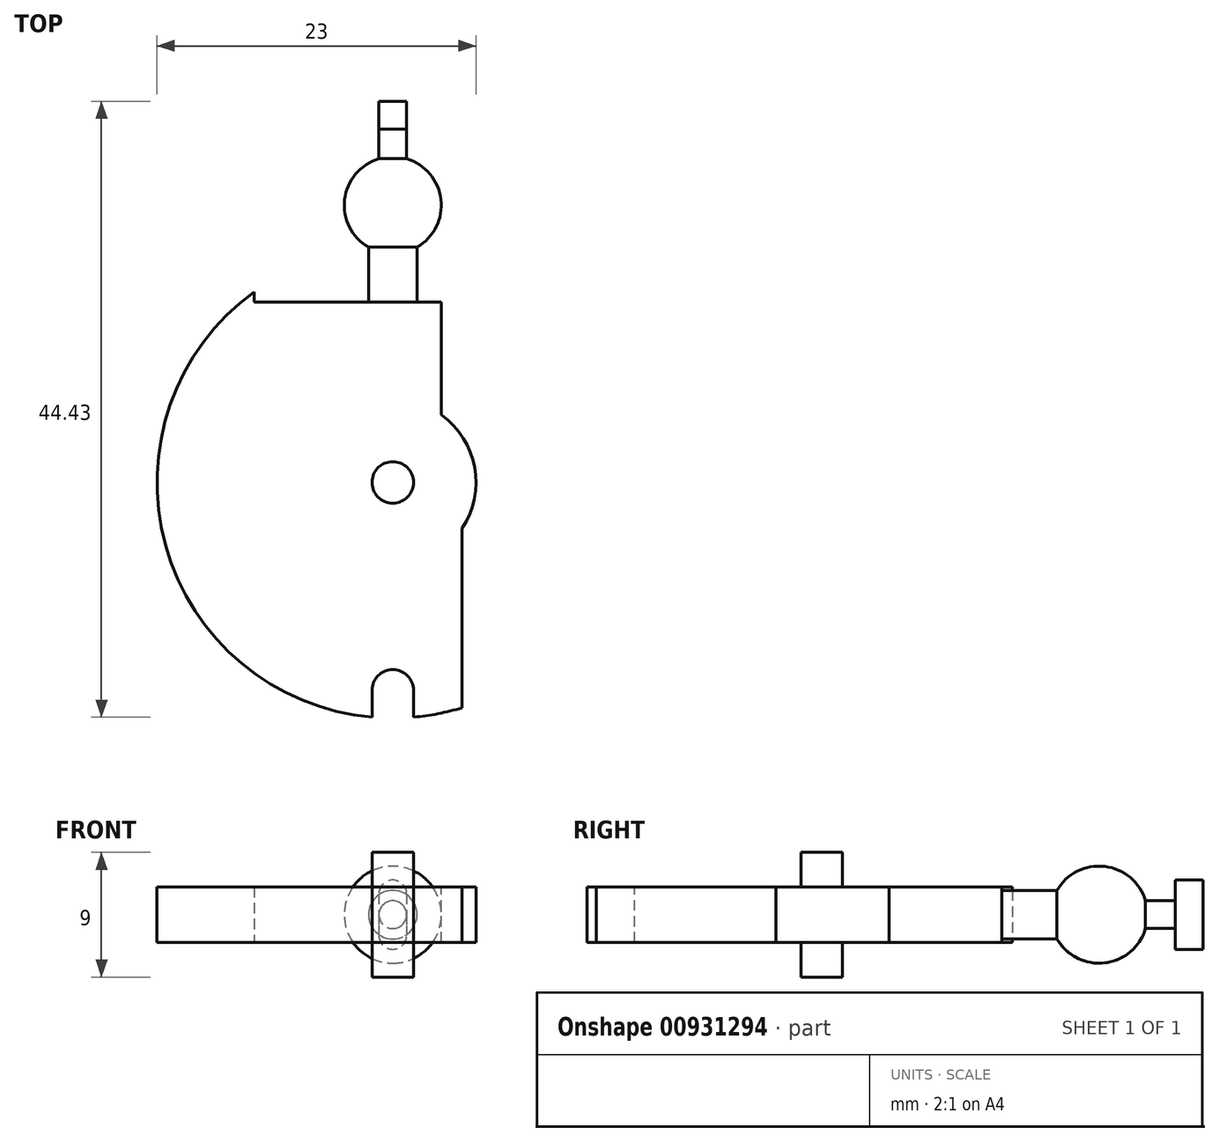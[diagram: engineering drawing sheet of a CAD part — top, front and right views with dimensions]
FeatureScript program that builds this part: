
annotation { "Feature Type Name" : "Feature", "Feature Type Description" : "" }
export const myFeature = defineFeature(function(context is Context, id is Id, definition is map)
    precondition{}
    {
        {
            var Q0;
            Q0=qCreatedBy(makeId("Top.planeOp"),FACE);
            var sketch = newSketch(context, id + "F0", { "sketchPlane" : qUnion([Q0])});
            skCircle(sketch, "E0", {"center": v(0, 0) * mm, "radius": 17 * mm});
            skSolve(sketch);
        }
        {
            var Q0;
            Q0=makeQuery(id+"F0.imprint","IMPRINT",FACE,{"disambiguationData":[TD([[makeQuery(id+"F0.imprint","IMPRINT",EDGE,{"derivedFrom":sQuery(id+"F0.wireOp",EDGE,"E0")}),1.0]])]});
            extrude(context, id + "F1", {"entities" : qUnion([Q0]), "endBound" : BoundingType.SYMMETRIC, "depth" : 4 * mm, "offsetDistance" : 25 * mm});
        }
        {
            var Q0;
            Q0=qCreatedBy(makeId("Top.planeOp"),FACE);
            var sketch = newSketch(context, id + "F2", { "sketchPlane" : qUnion([Q0])});
            skLineSegment(sketch, "E1", {"start": v(-18.14, 0) * mm, "end": v(21.61, 0) * mm, "construction": true});
            skLineSegment(sketch, "E2", {"start": v(0, 15.6) * mm, "end": v(0, -23.05) * mm, "construction": true});
            skLineSegment(sketch, "E3.bottom", {"start": v(5, 0) * mm, "end": v(35, 0) * mm});
            skLineSegment(sketch, "E3.top", {"start": v(5, -30) * mm, "end": v(35, -30) * mm});
            skLineSegment(sketch, "E3.left", {"start": v(5, 0) * mm, "end": v(5, -30) * mm});
            skLineSegment(sketch, "E3.right", {"start": v(35, 0) * mm, "end": v(35, -30) * mm});
            skSolve(sketch);
        }
        {
            var Q0;
            Q0=makeQuery(id+"F2.imprint","IMPRINT",FACE,{"disambiguationData":[TD([[makeQuery(id+"F2.imprint","IMPRINT",EDGE,{"derivedFrom":sQuery(id+"F2.wireOp",EDGE,"E3.bottom")}),-1.0]])]});
            extrude(context, id + "F3", {"entities" : qUnion([Q0]), "operationType" : NewBodyOperationType.REMOVE, "endBound" : BoundingType.SYMMETRIC, "oppositeDirection" : true, "depth" : 25 * mm, "offsetDistance" : 25 * mm});
        }
        {
            var Q0;
            Q0=qCreatedBy(makeId("Top.planeOp"),FACE);
            var sketch = newSketch(context, id + "F4", { "sketchPlane" : qUnion([Q0])});
            skLineSegment(sketch, "E4", {"start": v(-5.74, 0) * mm, "end": v(12.51, 0) * mm, "construction": true});
            skLineSegment(sketch, "E5", {"start": v(0, 9.37) * mm, "end": v(0, -3) * mm, "construction": true});
            skLineSegment(sketch, "E6.bottom", {"start": v(3.5, 30) * mm, "end": v(33.5, 30) * mm});
            skLineSegment(sketch, "E6.top", {"start": v(3.5, 0) * mm, "end": v(33.5, 0) * mm});
            skLineSegment(sketch, "E6.left", {"start": v(3.5, 30) * mm, "end": v(3.5, 0) * mm});
            skLineSegment(sketch, "E6.right", {"start": v(33.5, 30) * mm, "end": v(33.5, 0) * mm});
            skSolve(sketch);
        }
        {
            var Q0;
            Q0=makeQuery(id+"F4.imprint","IMPRINT",FACE,{"disambiguationData":[TD([[makeQuery(id+"F4.imprint","IMPRINT",EDGE,{"derivedFrom":sQuery(id+"F4.wireOp",EDGE,"E6.bottom")}),-1.0]])]});
            extrude(context, id + "F5", {"entities" : qUnion([Q0]), "operationType" : NewBodyOperationType.REMOVE, "endBound" : BoundingType.SYMMETRIC, "oppositeDirection" : true, "depth" : 25 * mm, "offsetDistance" : 25 * mm});
        }
        {
            var Q0;
            Q0=qCreatedBy(makeId("Top.planeOp"),FACE);
            var sketch = newSketch(context, id + "F6", { "sketchPlane" : qUnion([Q0])});
            skCircle(sketch, "E7", {"center": v(0, 0) * mm, "radius": 6 * mm});
            skSolve(sketch);
        }
        {
            var Q0;
            Q0=makeQuery(id+"F6.imprint","IMPRINT",FACE,{"disambiguationData":[TD([[makeQuery(id+"F6.imprint","IMPRINT",EDGE,{"derivedFrom":sQuery(id+"F6.wireOp",EDGE,"E7")}),1.0]])]});
            var Q1;
            Q1=makeQuery(id+"F1.opExtrude","CAP_FACE",FACE,{"disambiguationData":[OSD([sQuery(id+"F0.wireOp",EDGE,"E0")])],"isStart":false});
            var Q2;
            Q2=makeQuery(id+"F1.opExtrude","CAP_FACE",FACE,{"disambiguationData":[OSD([sQuery(id+"F0.wireOp",EDGE,"E0")])],"isStart":true});
            extrude(context, id + "F7", {"entities" : qUnion([Q0]), "operationType" : NewBodyOperationType.ADD, "endBound" : BoundingType.UP_TO_SURFACE, "depth" : 25 * mm, "endBoundEntityFace" : qUnion([Q1]), "offsetDistance" : 25 * mm, "hasSecondDirection" : true, "secondDirectionBound" : SecondDirectionBoundingType.UP_TO_SURFACE, "secondDirectionOppositeDirection" : true, "secondDirectionDepth" : 25 * mm, "secondDirectionBoundEntityFace" : qUnion([Q2])});
        }
        {
            var Q0;
            Q0=qCreatedBy(makeId("Top.planeOp"),FACE);
            var sketch = newSketch(context, id + "F8", { "sketchPlane" : qUnion([Q0])});
            skLineSegment(sketch, "E8", {"start": v(-24.74, 0) * mm, "end": v(14.33, 0) * mm, "construction": true});
            skLineSegment(sketch, "E9", {"start": v(0, 22.26) * mm, "end": v(0, -22.71) * mm, "construction": true});
            skLineSegment(sketch, "E10.bottom", {"start": v(-10, 18) * mm, "end": v(10, 18) * mm});
            skLineSegment(sketch, "E10.top", {"start": v(-10, 13) * mm, "end": v(10, 13) * mm});
            skLineSegment(sketch, "E10.left", {"start": v(-10, 18) * mm, "end": v(-10, 13) * mm});
            skLineSegment(sketch, "E10.right", {"start": v(10, 18) * mm, "end": v(10, 13) * mm});
            skSolve(sketch);
        }
        {
            var Q0;
            Q0=makeQuery(id+"F8.imprint","IMPRINT",FACE,{"disambiguationData":[TD([[makeQuery(id+"F8.imprint","IMPRINT",EDGE,{"derivedFrom":sQuery(id+"F8.wireOp",EDGE,"E10.bottom")}),-1.0]])]});
            extrude(context, id + "F9", {"entities" : qUnion([Q0]), "operationType" : NewBodyOperationType.REMOVE, "endBound" : BoundingType.SYMMETRIC, "oppositeDirection" : true, "depth" : 25 * mm, "offsetDistance" : 25 * mm});
        }
        {
            var Q0;
            Q0=qCreatedBy(makeId("Top.planeOp"),FACE);
            var sketch = newSketch(context, id + "F10", { "sketchPlane" : qUnion([Q0])});
            skCircle(sketch, "E11", {"center": v(0, 0) * mm, "radius": 1.5 * mm});
            skSolve(sketch);
        }
        {
            var Q0;
            Q0 = qSketchRegion(id + "F10", true);
            extrude(context, id + "F11", {"entities" : qUnion([Q0]), "operationType" : NewBodyOperationType.ADD, "endBound" : BoundingType.SYMMETRIC, "depth" : 9 * mm, "offsetDistance" : 25 * mm});
        }
        {
            var Q0;
            Q0=qCreatedBy(makeId("Top.planeOp"),FACE);
            var sketch = newSketch(context, id + "F12", { "sketchPlane" : qUnion([Q0])});
            skCircle(sketch, "E12", {"center": v(0, 20) * mm, "radius": 3.5 * mm});
            skLineSegment(sketch, "E13", {"start": v(0, 24.78) * mm, "end": v(0, -5.96) * mm, "construction": true});
            skLineSegment(sketch, "E14", {"start": v(-20.14, 0) * mm, "end": v(15.9, 0) * mm, "construction": true});
            skLineSegment(sketch, "E15", {"start": v(0, 15.3) * mm, "end": v(0, 24.28) * mm});
            skSolve(sketch);
        }
        {
            var Q0;
            {var subQ0=sQuery(id+"F12.wireOp",EDGE,"E15");var subQ1=sQuery(id+"F12.wireOp",EDGE,"E12");var subQ2=makeQuery(id+"F12.imprint","INTERSECT",VERTEX,{"disambiguationData":[OD(0.0)],"derivedFrom":[subQ1,subQ0]});Q0=makeQuery(id+"F12.imprint","IMPRINT",FACE,{"disambiguationData":[TD([[makeQuery(id+"F12.imprint","IMPRINT",EDGE,{"disambiguationData":[TD([[subQ2,1.0]])],"derivedFrom":subQ1}),1.0]])]});}
            var Q1;
            Q1=sQuery(id+"F12.wireOp",EDGE,"E15");
            revolve(context, id + "F13", {"operationType" : NewBodyOperationType.ADD, "surfaceOperationType" : NewSurfaceOperationType.NEW, "entities" : qUnion([Q0]), "axis" : qUnion([Q1]), "revolveType" : RevolveType.FULL});
        }
        {
            var Q0;
            Q0=qCreatedBy(makeId("Front.planeOp"),FACE);
            cPlane(context, id + "F14", {"entities" : qUnion([Q0]), "cplaneType" : CPlaneType.OFFSET, "offset" : 13 * mm, "oppositeDirection" : true, "width" : 150 * mm, "height" : 150 * mm});
        }
        {
            var Q0;
            Q0=qCreatedBy(id+"F14.planeOp",FACE);
            var sketch = newSketch(context, id + "F15", { "sketchPlane" : qUnion([Q0])});
            skCircle(sketch, "E16", {"center": v(0, 0) * mm, "radius": 1.75 * mm});
            skSolve(sketch);
        }
        {
            var Q0;
            Q0 = qSketchRegion(id + "F15", true);
            extrude(context, id + "F16", {"entities" : qUnion([Q0]), "operationType" : NewBodyOperationType.ADD, "endBound" : BoundingType.UP_TO_NEXT, "oppositeDirection" : true, "depth" : 25 * mm, "offsetDistance" : 25 * mm});
        }
        {
            var Q0;
            Q0=qCreatedBy(makeId("Front.planeOp"),FACE);
            cPlane(context, id + "F17", {"entities" : qUnion([Q0]), "cplaneType" : CPlaneType.OFFSET, "offset" : 25.5 * mm, "oppositeDirection" : true, "width" : 150 * mm, "height" : 150 * mm});
        }
        {
            var Q0;
            Q0=qCreatedBy(id+"F17.planeOp",FACE);
            var sketch = newSketch(context, id + "F18", { "sketchPlane" : qUnion([Q0])});
            skLineSegment(sketch, "E17", {"start": v(-5.83, 0) * mm, "end": v(7.58, 0) * mm, "construction": true});
            skLineSegment(sketch, "E18", {"start": v(0, 7.92) * mm, "end": v(0, -9.29) * mm, "construction": true});
            skLineSegment(sketch, "E19.bottom", {"start": v(-1, 2.5) * mm, "end": v(1, 2.5) * mm});
            skLineSegment(sketch, "E19.top", {"start": v(-1, -2.5) * mm, "end": v(1, -2.5) * mm});
            skLineSegment(sketch, "E19.left", {"start": v(-1, 2.5) * mm, "end": v(-1, -2.5) * mm});
            skLineSegment(sketch, "E19.right", {"start": v(1, 2.5) * mm, "end": v(1, -2.5) * mm});
            skSolve(sketch);
        }
        {
            var Q0;
            Q0 = qSketchRegion(id + "F18", true);
            extrude(context, id + "F19", {"entities" : qUnion([Q0]), "operationType" : NewBodyOperationType.ADD, "oppositeDirection" : true, "depth" : 2 * mm, "offsetDistance" : 25 * mm});
        }
        {
            var Q0;
            Q0=makeQuery(id+"F19.opExtrude","SWEPT_EDGE",EDGE,{"disambiguationData":[OSD([sQuery(id+"F18.wireOp",EDGE,"E19.bottom"),sQuery(id+"F18.wireOp",EDGE,"E19.right")])]});
            var Q1;
            Q1=makeQuery(id+"F19.opExtrude","SWEPT_EDGE",EDGE,{"disambiguationData":[OSD([sQuery(id+"F18.wireOp",EDGE,"E19.bottom"),sQuery(id+"F18.wireOp",EDGE,"E19.left")])]});
            var Q2;
            Q2=makeQuery(id+"F19.opExtrude","SWEPT_EDGE",EDGE,{"disambiguationData":[OSD([sQuery(id+"F18.wireOp",EDGE,"E19.top"),sQuery(id+"F18.wireOp",EDGE,"E19.left")])]});
            var Q3;
            Q3=makeQuery(id+"F19.opExtrude","SWEPT_EDGE",EDGE,{"disambiguationData":[OSD([sQuery(id+"F18.wireOp",EDGE,"E19.top"),sQuery(id+"F18.wireOp",EDGE,"E19.right")])]});
            fillet(context, id + "F20", {"entities" : qUnion([Q0, Q1, Q2, Q3]), "radius" : 1 * mm, "tangentPropagation" : true, "allowEdgeOverflow" : false});
        }
        {
            var Q0;
            Q0=qCreatedBy(id+"F17.planeOp",FACE);
            var sketch = newSketch(context, id + "F21", { "sketchPlane" : qUnion([Q0])});
            skCircle(sketch, "E20", {"center": v(0, 0) * mm, "radius": 1 * mm});
            skSolve(sketch);
        }
        {
            var Q0;
            Q0 = qSketchRegion(id + "F21", true);
            extrude(context, id + "F22", {"entities" : qUnion([Q0]), "operationType" : NewBodyOperationType.ADD, "endBound" : BoundingType.UP_TO_NEXT, "depth" : 25 * mm, "offsetDistance" : 25 * mm});
        }
        {
            var Q0;
            Q0=qCreatedBy(makeId("Top.planeOp"),FACE);
            var sketch = newSketch(context, id + "F23", { "sketchPlane" : qUnion([Q0])});
            skLineSegment(sketch, "E21", {"start": v(-7.13, 0) * mm, "end": v(5.6, 0) * mm, "construction": true});
            skLineSegment(sketch, "E22", {"start": v(0, 1.87) * mm, "end": v(0, -12.04) * mm, "construction": true});
            skLineSegment(sketch, "E23.top", {"start": v(-1.5, -20) * mm, "end": v(1.5, -20) * mm});
            skLineSegment(sketch, "E23.left", {"start": v(-1.5, -15) * mm, "end": v(-1.5, -20) * mm});
            skLineSegment(sketch, "E23.right", {"start": v(1.5, -15) * mm, "end": v(1.5, -20) * mm});
            skArc(sketch, "E24", {"start": v(1.5, -15) * mm, "mid": v(0, -13.5) * mm, "end": v(-1.5, -15) * mm});
            skSolve(sketch);
        }
        {
            var Q0;
            Q0=makeQuery(id+"F23.imprint","IMPRINT",FACE,{"disambiguationData":[TD([[makeQuery(id+"F23.imprint","IMPRINT",EDGE,{"derivedFrom":sQuery(id+"F23.wireOp",EDGE,"E23.top")}),1.0]])]});
            extrude(context, id + "F24", {"entities" : qUnion([Q0]), "operationType" : NewBodyOperationType.REMOVE, "endBound" : BoundingType.SYMMETRIC, "oppositeDirection" : true, "depth" : 25 * mm, "offsetDistance" : 25 * mm});
        }
    });
